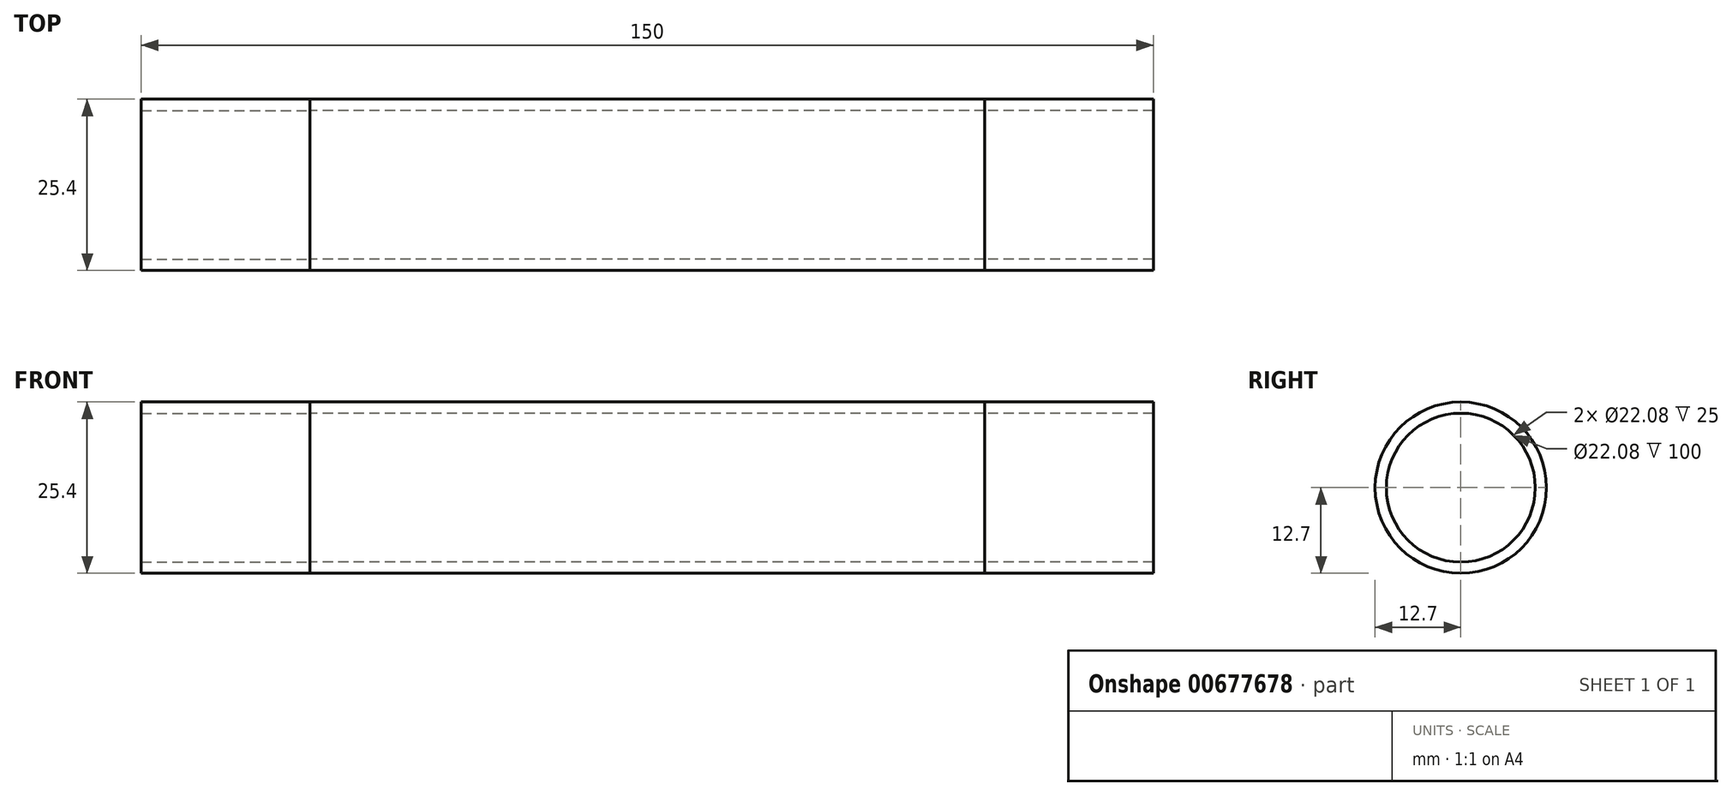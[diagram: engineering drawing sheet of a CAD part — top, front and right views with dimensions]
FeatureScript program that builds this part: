
annotation { "Feature Type Name" : "Feature", "Feature Type Description" : "" }
export const myFeature = defineFeature(function(context is Context, id is Id, definition is map)
    precondition{}
    {
        {
            var Q0;
            Q0=qCreatedBy(makeId("Right.planeOp"),FACE);
            var sketch = newSketch(context, id + "F0", { "sketchPlane" : qUnion([Q0])});
            skCircle(sketch, "E0", {"center": v(0, 0) * mm, "radius": 12.7 * mm});
            skCircle(sketch, "E1.0", {"center": v(0, 0) * mm, "radius": 11.04 * mm});
            skSolve(sketch);
        }
        {
            var Q0;
            Q0=makeQuery(id+"F0.imprint","IMPRINT",FACE,{"disambiguationData":[TD([[makeQuery(id+"F0.imprint","IMPRINT",EDGE,{"derivedFrom":sQuery(id+"F0.wireOp",EDGE,"E0")}),1.0]])]});
            extrude(context, id + "F1", {"entities" : qUnion([Q0]), "endBound" : BoundingType.SYMMETRIC, "depth" : 100 * mm, "offsetDistance" : 25 * mm});
        }
        {
            var Q0;
            Q0=makeQuery(id+"F1.opExtrude","CAP_FACE",FACE,{"disambiguationData":[OSD([sQuery(id+"F0.wireOp",EDGE,"E0"),sQuery(id+"F0.wireOp",EDGE,"E1.0")])],"isStart":false});
            extrude(context, id + "F2", {"entities" : qUnion([Q0]), "depth" : 25 * mm, "offsetDistance" : 25 * mm});
        }
        {
            var Q0;
            Q0=makeQuery(id+"F2.opExtrude","SWEPT_BODY",BODY,{"disambiguationData":[OSD([sQuery(id+"F0.wireOp",EDGE,"E0"),sQuery(id+"F0.wireOp",EDGE,"E1.0")])]});
            var Q1;
            Q1=qCreatedBy(makeId("Right.planeOp"),FACE);
            mirror(context, id + "F3", {"entities" : qUnion([Q0]), "mirrorPlane" : qUnion([Q1])});
        }
    });
